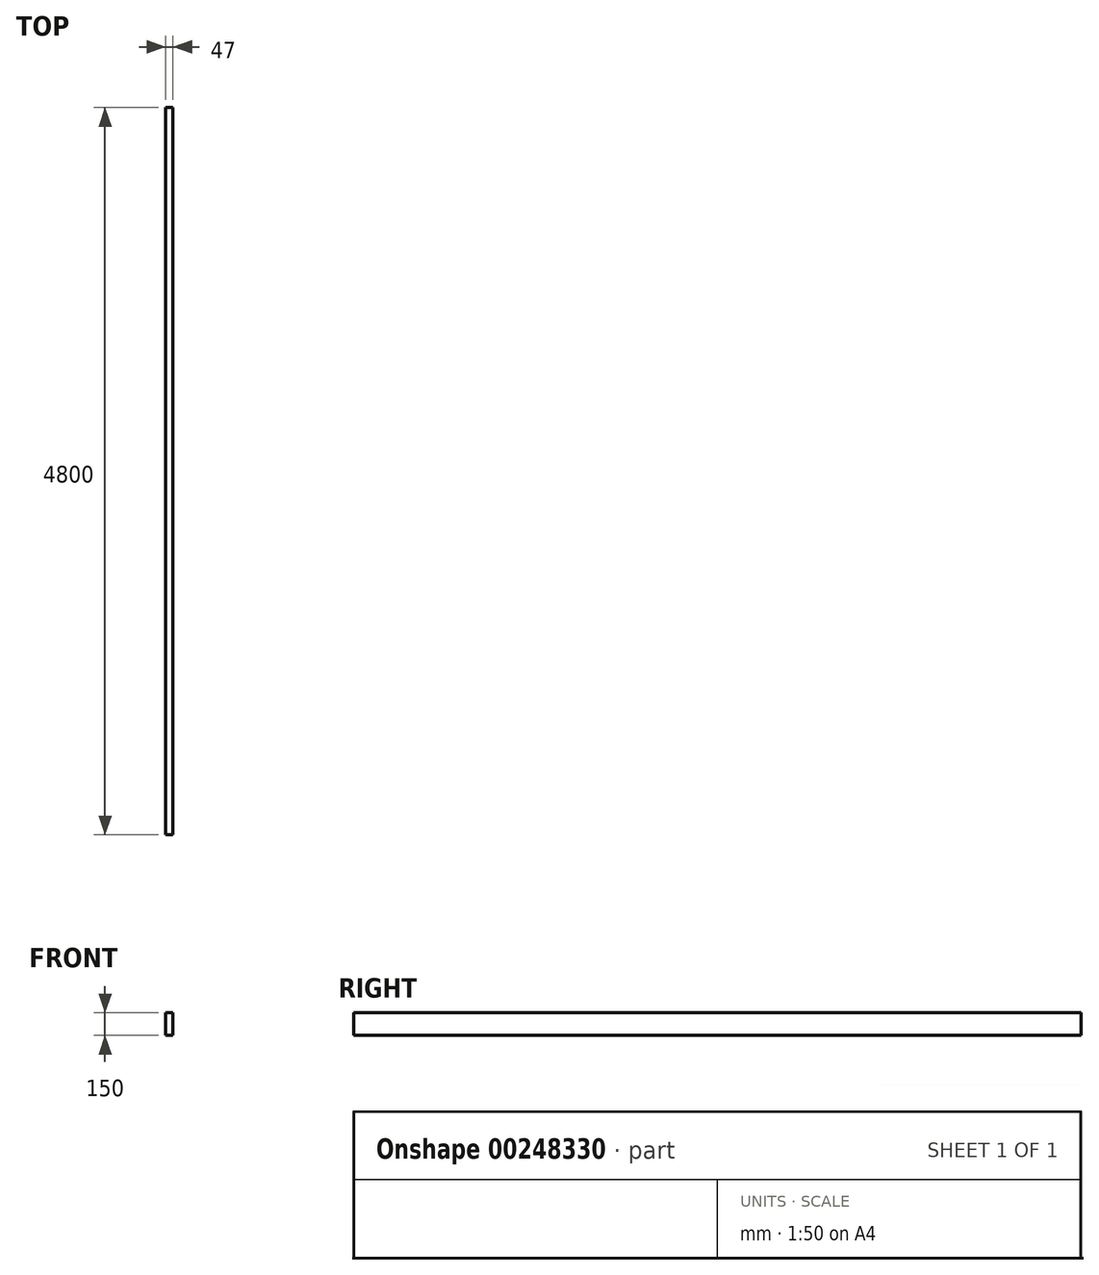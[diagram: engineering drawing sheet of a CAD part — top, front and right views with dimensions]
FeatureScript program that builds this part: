
annotation { "Feature Type Name" : "Feature", "Feature Type Description" : "" }
export const myFeature = defineFeature(function(context is Context, id is Id, definition is map)
    precondition{}
    {
        {
            var Q0;
            Q0=qCreatedBy(makeId("Front.planeOp"),FACE);
            var sketch = newSketch(context, id + "F0", { "sketchPlane" : qUnion([Q0])});
            skLineSegment(sketch, "E0.bottom", {"start": v(0, 0) * mm, "end": v(47, 0) * mm});
            skLineSegment(sketch, "E0.top", {"start": v(0, 150) * mm, "end": v(47, 150) * mm});
            skLineSegment(sketch, "E0.left", {"start": v(0, 0) * mm, "end": v(0, 150) * mm});
            skLineSegment(sketch, "E0.right", {"start": v(47, 0) * mm, "end": v(47, 150) * mm});
            skSolve(sketch);
        }
        {
            var Q0;
            Q0=makeQuery(id+"F0.imprint","IMPRINT",FACE,{"disambiguationData":[TD([[makeQuery(id+"F0.imprint","IMPRINT",EDGE,{"derivedFrom":sQuery(id+"F0.wireOp",EDGE,"E0.bottom")}),1.0]])]});
            extrude(context, id + "F1", {"entities" : qUnion([Q0]), "oppositeDirection" : true, "depth" : 4800 * mm});
        }
    });
